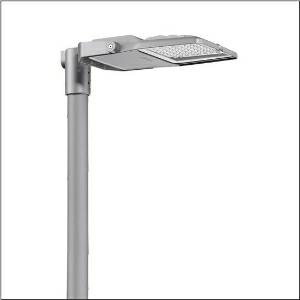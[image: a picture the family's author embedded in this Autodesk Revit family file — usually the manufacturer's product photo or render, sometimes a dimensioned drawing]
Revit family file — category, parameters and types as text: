
# Revit family: floodlight_fl_21_mini___pl64_5xa7772d2e3a_45b9
name_source: partatom
category: Lighting Fixtures
units: mm (PartAtom-declared; Revit-internal decimal feet)

## family parameters
Cut with Voids When Loaded = No
Host = Face
Light Source = No
Part Type = Normal
Room Calculation Point = No
Round Connector Dimension = Use Diameter
Shared = No

## types (1)
- --- (1 x LED, 17220 lm, 143 W, 3000K)
    Apparent Load = 143 VA
    CIE Flux Codes = 28 80 98 100 100
    Color Rendering = 70
    Color Temperature = 3000K
    Default Elevation = 1800 mm
    Description = Floodlight FL 21 mini, floodlight, primary light control with lens, of PMMA, primary optical cover: protective disc, of toughened safety glass, transparent, light distribution: PL64, light emission: direct distribution, installation type: surface-mounted, LED, High Power LED, rated luminous flux: 17.220lm, luminous efficacy: 120lm/W, light colour: 730, colour temperature: 3000K, control gear: ECG iQ, control: Auto-Match, Temp-Guard, Night-Set, Smart-Wire, Desk-Remote (wireless, voltage-free reading and setting of iQ features in the workshop via application-optimized NFC function/RFID function), optimised constant luminous flux control (CLO 2.0), Light-Fading, Lumen-Switch, with terminal, 6-pole, mains connection: 220..240V, AC, 50/60Hz, start of lifetime: 143W, end of lifetime: 152W, reduction: 61W, luminaire housing, of diecast aluminium, powder-coated, Siteco® metallic grey (DB 702S), corrosivity category C5 according to DIN EN ISO 12944, mast bracket, of steel, galvanised, powder-coated, protection rating (complete): IP66, insulation class (complete): insulation class II (safety insulation), certification: CE, ENEC, VDE, protection symbol: D, impact resistance: IK08, permissible operating ambient temperature: -40..+40°C, permissible operating ambient temperature for outdoor applications: -40..+50°C, standard: DIN EN 12944, packaging unit: 1 piece

Light Distribution: PL64
    Height = 70 mm
    Lamp = 1 x LED
    Lamp Light Flux = 17220 lm
    Lamp Power = 143 W
    Lamp count = 1
    Length = 485 mm
    Luminous efficacy = 120 lm/W
    Manufacturer = Siteco
    ModVariant = No
    Model = 5XA7772D2E3A
    Number of Poles = 1
    OnlyDefault = Yes
    Power Factor = 1
    Product Name = Floodlight FL 21 mini | PL64
    Product group = floodlight | pylon top
    ProductGroupID = 6101
    Protection Class = Protection class II
    Protection Degree = IP 66
    RLX_Detail_Level = 1
    RlxData = <blob elided: 101405 chars, md5=4b47c422>
    Socket = socket
    Standby Power = 0 W
    System Light Flux = 17220 lm
    System Power = 143 W
    Type Comments = factory setting: luminous flux: 100 % | dim-lin: 254 | 730 mA
    Type Image = l_1007125.jpg
    URL = http://relux.com
    VarID = @adj_076853
    Voltage = 0 V
    Weight = 0.00 kg
    Width = 337 mm

## geometry (parser evidence)
native form markers: Blend x4, Sweep x11
no freeform markers — native parametric forms only
